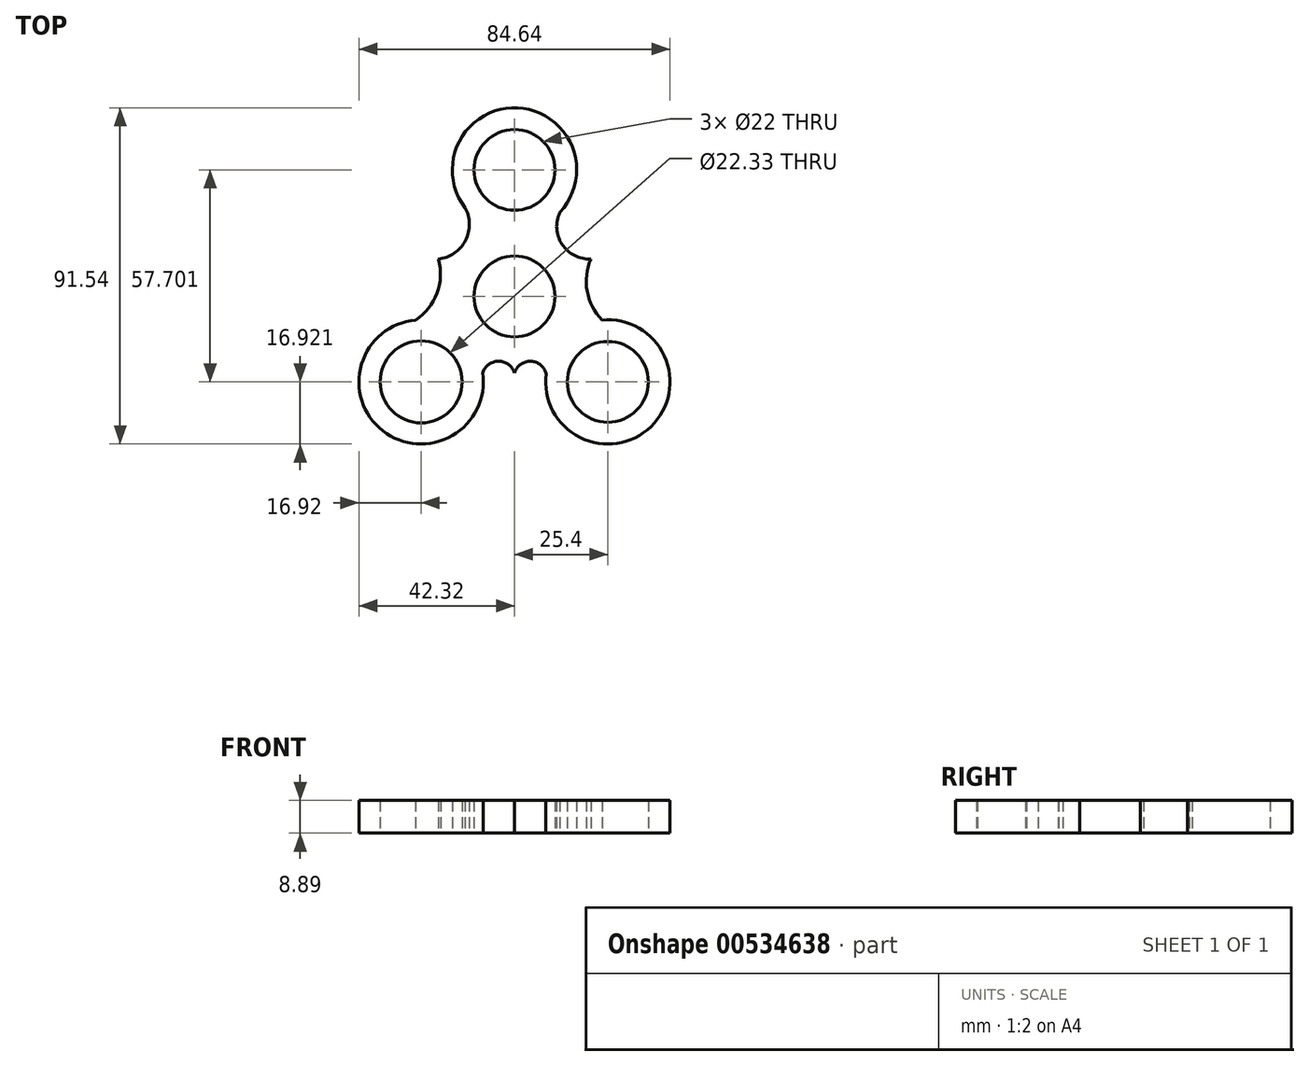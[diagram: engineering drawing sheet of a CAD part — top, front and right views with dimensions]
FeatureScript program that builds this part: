
annotation { "Feature Type Name" : "Feature", "Feature Type Description" : "" }
export const myFeature = defineFeature(function(context is Context, id is Id, definition is map)
    precondition{}
    {
        {
            var Q0;
            Q0=qCreatedBy(makeId("Top.planeOp"),FACE);
            var sketch = newSketch(context, id + "F0", { "sketchPlane" : qUnion([Q0])});
            skCircle(sketch, "E0", {"center": v(0, 0) * mm, "radius": 11 * mm});
            skCircle(sketch, "E1", {"center": v(0, 34.44) * mm, "radius": 11 * mm});
            skCircle(sketch, "E2", {"center": v(-25.4, -23.26) * mm, "radius": 11 * mm});
            skCircle(sketch, "E3", {"center": v(25.4, -23.26) * mm, "radius": 11 * mm});
            skPoint(sketch, "E4.orphan", {"position": v(0, -23.26) * mm});
            skCircle(sketch, "E5", {"center": v(-25.4, -23.26) * mm, "radius": 11.16 * mm});
            skPoint(sketch, "E6.endSnap0", {"position": v(47.68, -29.56) * mm});
            skPoint(sketch, "E6.end.orphan", {"position": v(47.68, -11.16) * mm});
            skPoint(sketch, "E7.start.orphan", {"position": v(-20.15, 4.63) * mm});
            skPoint(sketch, "E8.start.orphan", {"position": v(21.38, 4.63) * mm});
            skPoint(sketch, "E9.end.orphan", {"position": v(52.03, -24.78) * mm});
            skPoint(sketch, "E10.start.orphan", {"position": v(26.35, 0) * mm});
            skPoint(sketch, "E11.center.orphan", {"position": v(-24.74, -24.78) * mm});
            skPoint(sketch, "E12.end.orphan", {"position": v(-20.47, 34.44) * mm});
            skArc(sketch, "E13", {"start": v(12.38, 22.91) * mm, "mid": v(0.83, 51.34) * mm, "end": v(-13.45, 24.18) * mm});
            skArc(sketch, "E14", {"start": v(-26.92, -6.41) * mm, "mid": v(-35.88, -36.54) * mm, "end": v(-8.66, -20.8) * mm});
            skArc(sketch, "E15", {"start": v(8.62, -21.1) * mm, "mid": v(37.15, -35.43) * mm, "end": v(23.82, -6.42) * mm});
            skArc(sketch, "E16", {"start": v(12.38, 22.91) * mm, "mid": v(12.96, 14.15) * mm, "end": v(20.78, 10.18) * mm});
            skArc(sketch, "E17", {"start": v(20.78, 10.18) * mm, "mid": v(19.78, 1.42) * mm, "end": v(23.82, -6.42) * mm});
            skArc(sketch, "E18", {"start": v(-20.67, 10.18) * mm, "mid": v(-13.32, 15.25) * mm, "end": v(-13.45, 24.18) * mm});
            skArc(sketch, "E19", {"start": v(-26.92, -6.41) * mm, "mid": v(-21.08, 0.86) * mm, "end": v(-20.67, 10.18) * mm});
            skArc(sketch, "E20", {"start": v(0, -20.8) * mm, "mid": v(-4.33, -17.63) * mm, "end": v(-8.66, -20.8) * mm});
            skArc(sketch, "E21", {"start": v(8.62, -21.1) * mm, "mid": v(4.42, -17.66) * mm, "end": v(0, -20.8) * mm});
            skSolve(sketch);
        }
        {
            var Q0;
            Q0 = qSketchRegion(id + "F0", true);
            extrude(context, id + "F1", {"entities" : qUnion([Q0]), "depth" : 8.9 * mm, "offsetDistance" : 25.4 * mm});
        }
    });
